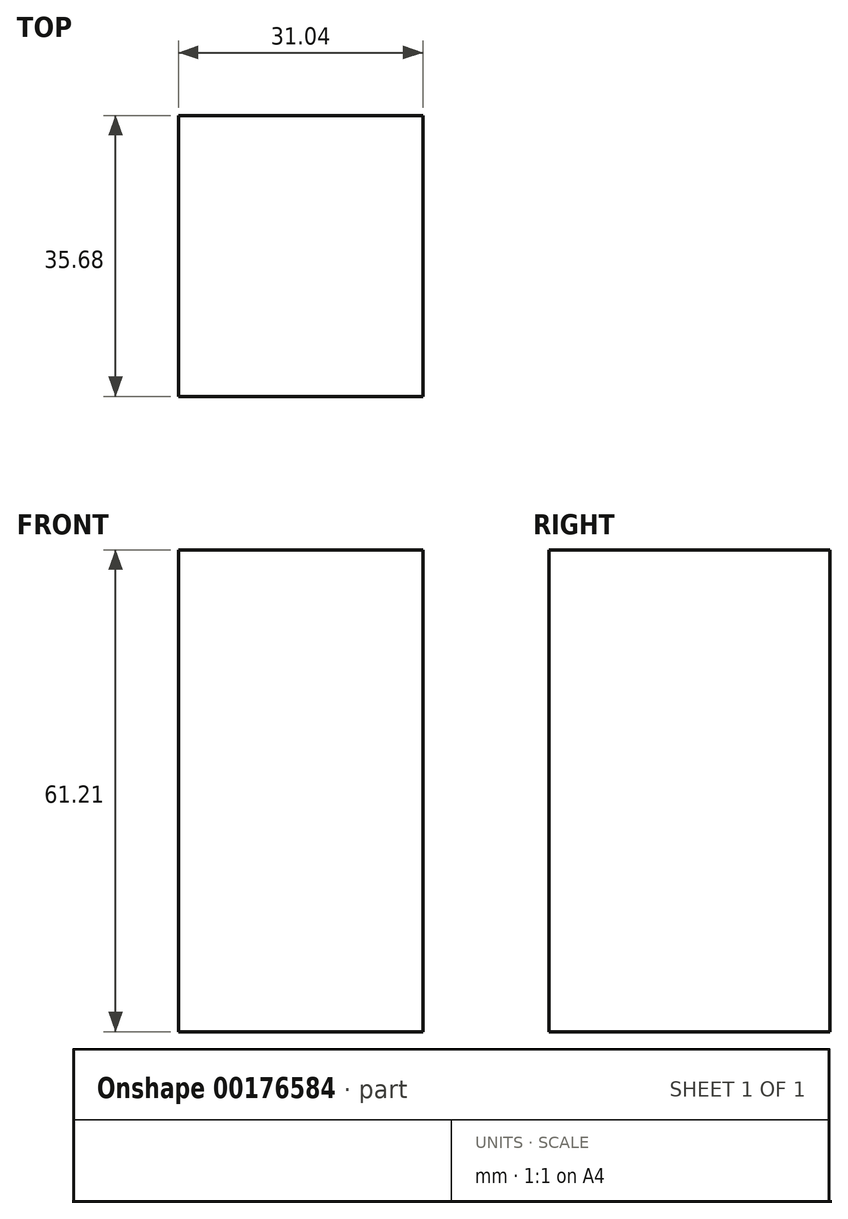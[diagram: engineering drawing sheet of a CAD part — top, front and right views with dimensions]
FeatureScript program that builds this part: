
annotation { "Feature Type Name" : "Feature", "Feature Type Description" : "" }
export const myFeature = defineFeature(function(context is Context, id is Id, definition is map)
    precondition{}
    {
        {
            var Q0;
            Q0=qCreatedBy(makeId("Top.planeOp"),FACE);
            var sketch = newSketch(context, id + "F0", { "sketchPlane" : qUnion([Q0])});
            skCircle(sketch, "E0", {"center": v(0, 0) * mm, "radius": 47.29 * mm});
            skLineSegment(sketch, "E1.bottom", {"start": v(0, 0) * mm, "end": v(31.04, 0) * mm});
            skLineSegment(sketch, "E1.top", {"start": v(0, -35.68) * mm, "end": v(31.04, -35.68) * mm});
            skLineSegment(sketch, "E1.left", {"start": v(0, 0) * mm, "end": v(0, -35.68) * mm});
            skLineSegment(sketch, "E1.right", {"start": v(31.04, 0) * mm, "end": v(31.04, -35.68) * mm});
            skSolve(sketch);
        }
        {
            var Q0;
            Q0=makeQuery(id+"F0.imprint","IMPRINT",FACE,{"disambiguationData":[TD([[makeQuery(id+"F0.imprint","IMPRINT",EDGE,{"derivedFrom":sQuery(id+"F0.wireOp",EDGE,"E1.bottom")}),-1.0]])]});
            extrude(context, id + "F1", {"entities" : qUnion([Q0]), "depth" : 61.2 * mm});
        }
    });
